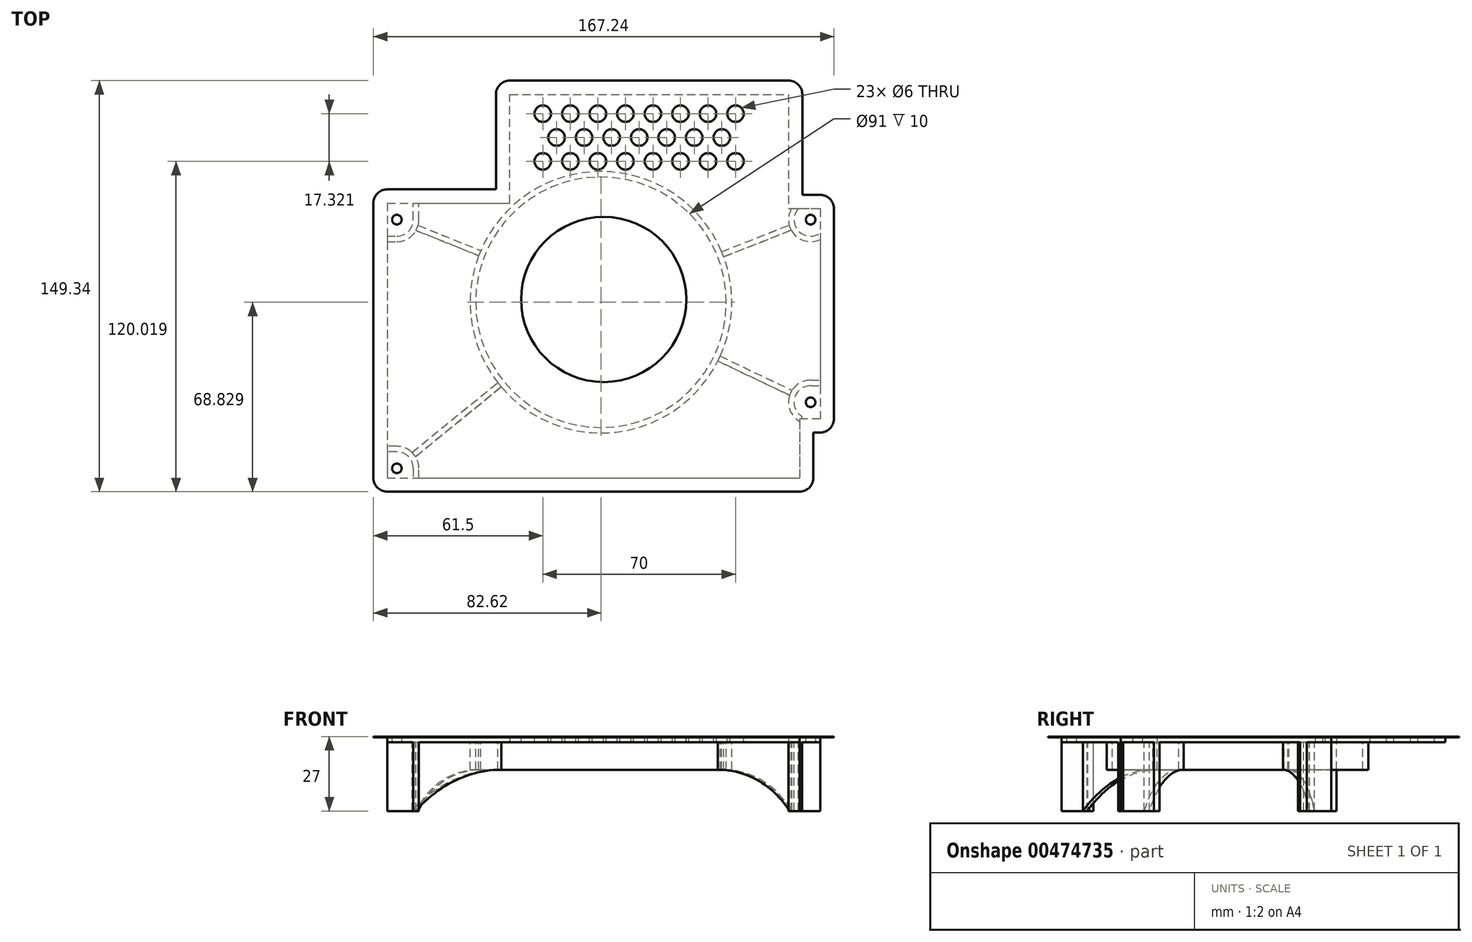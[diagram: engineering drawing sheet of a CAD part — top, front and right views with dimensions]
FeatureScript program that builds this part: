
annotation { "Feature Type Name" : "Feature", "Feature Type Description" : "" }
export const myFeature = defineFeature(function(context is Context, id is Id, definition is map)
    precondition{}
    {
        {
            var Q0;
            Q0=qCreatedBy(makeId("Top.planeOp"),FACE);
            var sketch = newSketch(context, id + "F0", { "sketchPlane" : qUnion([Q0])});
            skLineSegment(sketch, "E0.bottom", {"start": v(0, 0) * mm, "end": v(158.24, 0) * mm, "construction": true});
            skLineSegment(sketch, "E0.top", {"start": v(0, 140.34) * mm, "end": v(158.24, 140.34) * mm, "construction": true});
            skLineSegment(sketch, "E0.left", {"start": v(0, 0) * mm, "end": v(0, 140.34) * mm, "construction": true});
            skLineSegment(sketch, "E0.right", {"start": v(158.24, 0) * mm, "end": v(158.24, 140.34) * mm, "construction": true});
            skLineSegment(sketch, "E1.bottom", {"start": v(45, 139.84) * mm, "end": v(146.24, 139.84) * mm});
            skLineSegment(sketch, "E1.top", {"start": v(0.5, 0.5) * mm, "end": v(150.24, 0.5) * mm});
            skLineSegment(sketch, "E1.left", {"start": v(0.5, 100.34) * mm, "end": v(0.5, 0.5) * mm});
            skLineSegment(sketch, "E1.right", {"start": v(157.74, 98.34) * mm, "end": v(157.74, 22) * mm});
            skCircle(sketch, "E2", {"center": v(4, 94.34) * mm, "radius": 1.75 * mm});
            skCircle(sketch, "E3", {"center": v(4, 4) * mm, "radius": 1.75 * mm});
            skCircle(sketch, "E4", {"center": v(154.24, 94.34) * mm, "radius": 1.75 * mm});
            skCircle(sketch, "E5", {"center": v(154.24, 28) * mm, "radius": 1.75 * mm});
            skLineSegment(sketch, "E6", {"start": v(157.74, 22) * mm, "end": v(150.24, 22) * mm});
            skLineSegment(sketch, "E7", {"start": v(150.24, 22) * mm, "end": v(150.24, 0.5) * mm});
            skLineSegment(sketch, "E8", {"start": v(146.24, 139.84) * mm, "end": v(146.24, 98.34) * mm});
            skLineSegment(sketch, "E9", {"start": v(146.24, 98.34) * mm, "end": v(157.74, 98.34) * mm});
            skLineSegment(sketch, "E10", {"start": v(0.5, 100.34) * mm, "end": v(45, 100.34) * mm});
            skLineSegment(sketch, "E11", {"start": v(45, 100.34) * mm, "end": v(45, 139.84) * mm});
            skCircle(sketch, "E12", {"center": v(79.12, 65.33) * mm, "radius": 44.5 * mm, "construction": true});
            skSolve(sketch);
        }
        {
            var Q0;
            Q0=qSketchRegion(id+"F0",true);
            extrude(context, id + "F1", {"entities" : qUnion([Q0]), "depth" : 2 * mm, "offsetDistance" : 25 * mm});
        }
        {
            var Q0;
            Q0=makeQuery(id+"F1.opExtrude","CAP_FACE",FACE,{"disambiguationData":[OSD([sQuery(id+"F0.wireOp",EDGE,"E1.bottom"),sQuery(id+"F0.wireOp",EDGE,"E1.top"),sQuery(id+"F0.wireOp",EDGE,"E1.left"),sQuery(id+"F0.wireOp",EDGE,"E1.right"),sQuery(id+"F0.wireOp",EDGE,"E2"),sQuery(id+"F0.wireOp",EDGE,"E3"),sQuery(id+"F0.wireOp",EDGE,"E4"),sQuery(id+"F0.wireOp",EDGE,"E5"),sQuery(id+"F0.wireOp",EDGE,"E6"),sQuery(id+"F0.wireOp",EDGE,"E7"),sQuery(id+"F0.wireOp",EDGE,"E8"),sQuery(id+"F0.wireOp",EDGE,"E9"),sQuery(id+"F0.wireOp",EDGE,"E10"),sQuery(id+"F0.wireOp",EDGE,"E11")])],"isStart":true});
            var sketch = newSketch(context, id + "F2", { "sketchPlane" : qUnion([Q0])});
            skCircle(sketch, "E13", {"center": v(78.12, -64.33) * mm, "radius": 44.5 * mm, "construction": true});
            skCircle(sketch, "E14", {"center": v(78.12, -64.33) * mm, "radius": 45.5 * mm});
            skLineSegment(sketch, "E15", {"start": v(120.56, -139.84) * mm, "end": v(122.87, -139.84) * mm});
            skLineSegment(sketch, "E16", {"start": v(4, -94.34) * mm, "end": v(78.12, -64.33) * mm, "construction": true});
            skLineSegment(sketch, "E17", {"start": v(4, -4) * mm, "end": v(78.12, -64.33) * mm, "construction": true});
            skLineSegment(sketch, "E18", {"start": v(154.24, -28) * mm, "end": v(78.12, -64.33) * mm, "construction": true});
            skLineSegment(sketch, "E19", {"start": v(78.12, -64.33) * mm, "end": v(154.24, -94.34) * mm, "construction": true});
            skArc(sketch, "E20", {"start": v(4, -10) * mm, "mid": v(8.24, -8.24) * mm, "end": v(10, -4) * mm});
            skArc(sketch, "E21", {"start": v(40.66, -35.13) * mm, "mid": v(31.15, -57.27) * mm, "end": v(33.73, -81.22) * mm});
            skArc(sketch, "E22", {"start": v(4, -12) * mm, "mid": v(6.98, -11.43) * mm, "end": v(9.52, -9.79) * mm});
            skLineSegment(sketch, "E23", {"start": v(10.79, -8.23) * mm, "end": v(41.92, -33.58) * mm});
            skLineSegment(sketch, "E24", {"start": v(9.52, -9.79) * mm, "end": v(40.66, -35.13) * mm});
            skArc(sketch, "E25.trimOffspring", {"start": v(10.79, -8.23) * mm, "mid": v(11.7, -6.2) * mm, "end": v(12, -4) * mm});
            skArc(sketch, "E26", {"start": v(10, -94.34) * mm, "mid": v(8.24, -90.1) * mm, "end": v(4, -88.34) * mm});
            skLineSegment(sketch, "E27", {"start": v(4, -10) * mm, "end": v(0.5, -10) * mm});
            skLineSegment(sketch, "E28", {"start": v(4, -12) * mm, "end": v(0.5, -12) * mm});
            skLineSegment(sketch, "E29", {"start": v(0.5, -10) * mm, "end": v(0.5, -12) * mm});
            skLineSegment(sketch, "E30", {"start": v(10, -4) * mm, "end": v(10, -0.5) * mm});
            skLineSegment(sketch, "E31", {"start": v(12, -0.5) * mm, "end": v(12, -4) * mm});
            skLineSegment(sketch, "E32", {"start": v(10, -0.5) * mm, "end": v(12, -0.5) * mm});
            skLineSegment(sketch, "E33", {"start": v(0.5, -86.34) * mm, "end": v(4, -86.34) * mm});
            skLineSegment(sketch, "E34", {"start": v(0.5, -88.34) * mm, "end": v(4, -88.34) * mm});
            skLineSegment(sketch, "E35", {"start": v(12, -94.34) * mm, "end": v(12, -100.34) * mm});
            skLineSegment(sketch, "E36", {"start": v(10, -94.34) * mm, "end": v(10, -100.34) * mm});
            skArc(sketch, "E37.trimOffspring", {"start": v(12, -94.34) * mm, "mid": v(11.93, -93.3) * mm, "end": v(11.73, -92.29) * mm});
            skLineSegment(sketch, "E38", {"start": v(0.5, -86.34) * mm, "end": v(0.5, -88.34) * mm});
            skLineSegment(sketch, "E39", {"start": v(10, -100.34) * mm, "end": v(12, -100.34) * mm});
            skLineSegment(sketch, "E40", {"start": v(10.98, -90.43) * mm, "end": v(33.73, -81.22) * mm});
            skLineSegment(sketch, "E41", {"start": v(11.73, -92.29) * mm, "end": v(34.48, -83.08) * mm});
            skArc(sketch, "E42.trimOffspring", {"start": v(10.98, -90.43) * mm, "mid": v(8.05, -87.44) * mm, "end": v(4, -86.34) * mm});
            skArc(sketch, "E43.trimOffspring", {"start": v(34.48, -83.08) * mm, "mid": v(78.34, -111.83) * mm, "end": v(121.93, -82.68) * mm});
            skArc(sketch, "E44", {"start": v(151.17, -22.85) * mm, "mid": v(148.46, -29.6) * mm, "end": v(154.24, -34) * mm});
            skArc(sketch, "E45", {"start": v(150.24, -21.07) * mm, "mid": v(146.76, -25.15) * mm, "end": v(146.65, -30.52) * mm});
            skLineSegment(sketch, "E46", {"start": v(154.24, -34) * mm, "end": v(157.74, -34) * mm});
            skLineSegment(sketch, "E47", {"start": v(154.24, -36) * mm, "end": v(157.74, -36) * mm});
            skLineSegment(sketch, "E48", {"start": v(157.74, -34) * mm, "end": v(157.74, -36) * mm});
            skLineSegment(sketch, "E49", {"start": v(150.24, -21.07) * mm, "end": v(150.24, -22) * mm});
            skLineSegment(sketch, "E50", {"start": v(150.24, -22) * mm, "end": v(151.17, -22) * mm});
            skLineSegment(sketch, "E51", {"start": v(120.55, -42.97) * mm, "end": v(146.65, -30.52) * mm});
            skLineSegment(sketch, "E52", {"start": v(121.4, -44.78) * mm, "end": v(147.5, -32.32) * mm});
            skArc(sketch, "E53.trimOffspring", {"start": v(120.55, -42.97) * mm, "mid": v(83.76, -17.16) * mm, "end": v(41.92, -33.58) * mm});
            skArc(sketch, "E54.trimOffspring", {"start": v(147.5, -32.32) * mm, "mid": v(150.4, -35.02) * mm, "end": v(154.24, -36) * mm});
            skArc(sketch, "E55", {"start": v(157.74, -89.47) * mm, "mid": v(149.78, -90.33) * mm, "end": v(149.77, -98.34) * mm});
            skArc(sketch, "E56", {"start": v(157.74, -87.15) * mm, "mid": v(151.81, -86.72) * mm, "end": v(147.22, -90.5) * mm});
            skLineSegment(sketch, "E57", {"start": v(147.31, -98.34) * mm, "end": v(149.77, -98.34) * mm});
            skLineSegment(sketch, "E58", {"start": v(157.74, -89.47) * mm, "end": v(157.74, -87.15) * mm});
            skLineSegment(sketch, "E59", {"start": v(122.67, -80.82) * mm, "end": v(147.22, -90.5) * mm});
            skLineSegment(sketch, "E60", {"start": v(121.93, -82.68) * mm, "end": v(146.49, -92.36) * mm});
            skArc(sketch, "E61.trimOffspring", {"start": v(122.67, -80.82) * mm, "mid": v(125.6, -62.67) * mm, "end": v(121.4, -44.78) * mm});
            skArc(sketch, "E62.trimOffspring", {"start": v(146.49, -92.36) * mm, "mid": v(146.31, -95.43) * mm, "end": v(147.31, -98.34) * mm});
            skLineSegment(sketch, "E63", {"start": v(151.17, -22) * mm, "end": v(151.17, -22.85) * mm});
            skSolve(sketch);
        }
        {
            var Q0;
            Q0=qSketchRegion(id+"F2",true);
            extrude(context, id + "F3", {"entities" : qUnion([Q0]), "operationType" : NewBodyOperationType.ADD, "depth" : 25 * mm, "offsetDistance" : 25 * mm});
        }
        {
            var Q0;
            Q0=makeQuery(id+"F3.opExtrude","CAP_FACE",FACE,{"disambiguationData":[OSD([sQuery(id+"F2.wireOp",EDGE,"E14"),sQuery(id+"F2.wireOp",EDGE,"E20"),sQuery(id+"F2.wireOp",EDGE,"E21"),sQuery(id+"F2.wireOp",EDGE,"E22"),sQuery(id+"F2.wireOp",EDGE,"E23"),sQuery(id+"F2.wireOp",EDGE,"E24"),sQuery(id+"F2.wireOp",EDGE,"E25.trimOffspring"),sQuery(id+"F2.wireOp",EDGE,"E26"),sQuery(id+"F2.wireOp",EDGE,"E27"),sQuery(id+"F2.wireOp",EDGE,"E28"),sQuery(id+"F2.wireOp",EDGE,"E29"),sQuery(id+"F2.wireOp",EDGE,"E30"),sQuery(id+"F2.wireOp",EDGE,"E31"),sQuery(id+"F2.wireOp",EDGE,"E32"),sQuery(id+"F2.wireOp",EDGE,"E33"),sQuery(id+"F2.wireOp",EDGE,"E34"),sQuery(id+"F2.wireOp",EDGE,"E35"),sQuery(id+"F2.wireOp",EDGE,"E36"),sQuery(id+"F2.wireOp",EDGE,"E37.trimOffspring"),sQuery(id+"F2.wireOp",EDGE,"E38"),sQuery(id+"F2.wireOp",EDGE,"E39"),sQuery(id+"F2.wireOp",EDGE,"E40"),sQuery(id+"F2.wireOp",EDGE,"E41"),sQuery(id+"F2.wireOp",EDGE,"E42.trimOffspring"),sQuery(id+"F2.wireOp",EDGE,"E43.trimOffspring"),sQuery(id+"F2.wireOp",EDGE,"E44"),sQuery(id+"F2.wireOp",EDGE,"E45"),sQuery(id+"F2.wireOp",EDGE,"E46"),sQuery(id+"F2.wireOp",EDGE,"E47"),sQuery(id+"F2.wireOp",EDGE,"E48"),sQuery(id+"F2.wireOp",EDGE,"E49"),sQuery(id+"F2.wireOp",EDGE,"E50"),sQuery(id+"F2.wireOp",EDGE,"E51"),sQuery(id+"F2.wireOp",EDGE,"E52"),sQuery(id+"F2.wireOp",EDGE,"E53.trimOffspring"),sQuery(id+"F2.wireOp",EDGE,"E54.trimOffspring"),sQuery(id+"F2.wireOp",EDGE,"E55"),sQuery(id+"F2.wireOp",EDGE,"E56"),sQuery(id+"F2.wireOp",EDGE,"E57"),sQuery(id+"F2.wireOp",EDGE,"E58"),sQuery(id+"F2.wireOp",EDGE,"E59"),sQuery(id+"F2.wireOp",EDGE,"E60"),sQuery(id+"F2.wireOp",EDGE,"E61.trimOffspring"),sQuery(id+"F2.wireOp",EDGE,"E62.trimOffspring"),sQuery(id+"F2.wireOp",EDGE,"E63")])],"isStart":false});
            var sketch = newSketch(context, id + "F4", { "sketchPlane" : qUnion([Q0])});
            skCircle(sketch, "E64", {"center": v(78.12, -64.33) * mm, "radius": 45.5 * mm});
            skCircle(sketch, "E65", {"center": v(78.12, -64.33) * mm, "radius": 47.5 * mm});
            skSolve(sketch);
        }
        {
            var Q0;
            Q0=qSketchRegion(id+"F4",true);
            extrude(context, id + "F5", {"entities" : qUnion([Q0]), "operationType" : NewBodyOperationType.REMOVE, "oppositeDirection" : true, "depth" : 15 * mm, "offsetDistance" : 25 * mm});
        }
        {
            var Q0;
            Q0=makeQuery(id+"F3.opExtrude","SWEPT_FACE",FACE,{"disambiguationData":[OSD([sQuery(id+"F2.wireOp",EDGE,"E24")])]});
            var sketch = newSketch(context, id + "F6", { "sketchPlane" : qUnion([Q0])});
            skArc(sketch, "E66", {"start": v(-13.56, -25) * mm, "mid": v(-32.28, -13.87) * mm, "end": v(-53.7, -10) * mm});
            skLineSegment(sketch, "E67", {"start": v(-53.7, -10) * mm, "end": v(-13.56, -10) * mm, "construction": true});
            skLineSegment(sketch, "E68", {"start": v(-53.7, -10) * mm, "end": v(-53.7, -25) * mm});
            skLineSegment(sketch, "E69", {"start": v(-53.7, -25) * mm, "end": v(-13.56, -25) * mm});
            skSolve(sketch);
        }
        {
            var Q0;
            Q0=qSketchRegion(id+"F6",true);
            extrude(context, id + "F7", {"entities" : qUnion([Q0]), "operationType" : NewBodyOperationType.REMOVE, "endBound" : BoundingType.UP_TO_NEXT, "oppositeDirection" : true, "depth" : 25 * mm, "offsetDistance" : 25 * mm});
        }
        {
            var Q0;
            Q0=makeQuery(id+"F3.opExtrude","SWEPT_FACE",FACE,{"disambiguationData":[OSD([sQuery(id+"F2.wireOp",EDGE,"E41")])]});
            var sketch = newSketch(context, id + "F8", { "sketchPlane" : qUnion([Q0])});
            skArc(sketch, "E70", {"start": v(23.76, -25) * mm, "mid": v(13.6, -14.05) * mm, "end": v(-0.78, -10) * mm});
            skLineSegment(sketch, "E71", {"start": v(-0.78, -10) * mm, "end": v(23.76, -10) * mm, "construction": true});
            skLineSegment(sketch, "E72", {"start": v(23.76, -25) * mm, "end": v(-0.78, -25) * mm});
            skLineSegment(sketch, "E73", {"start": v(-0.78, -25) * mm, "end": v(-0.78, -10) * mm});
            skSolve(sketch);
        }
        {
            var Q0;
            Q0=qSketchRegion(id+"F8",true);
            extrude(context, id + "F9", {"entities" : qUnion([Q0]), "operationType" : NewBodyOperationType.REMOVE, "endBound" : BoundingType.UP_TO_NEXT, "oppositeDirection" : true, "depth" : 25 * mm, "offsetDistance" : 25 * mm});
        }
        {
            var Q0;
            Q0=makeQuery(id+"F3.opExtrude","SWEPT_FACE",FACE,{"disambiguationData":[OSD([sQuery(id+"F2.wireOp",EDGE,"E60")])]});
            var sketch = newSketch(context, id + "F10", { "sketchPlane" : qUnion([Q0])});
            skLineSegment(sketch, "E74", {"start": v(-143.76, -10) * mm, "end": v(-143.76, -25) * mm});
            skLineSegment(sketch, "E75", {"start": v(-143.76, -25) * mm, "end": v(-170.16, -25) * mm});
            skLineSegment(sketch, "E76", {"start": v(-143.76, -10) * mm, "end": v(-170.16, -10) * mm, "construction": true});
            skArc(sketch, "E77", {"start": v(-143.76, -10) * mm, "mid": v(-158.94, -14.01) * mm, "end": v(-170.16, -25) * mm});
            skSolve(sketch);
        }
        {
            var Q0;
            Q0=qSketchRegion(id+"F10",true);
            extrude(context, id + "F11", {"entities" : qUnion([Q0]), "operationType" : NewBodyOperationType.REMOVE, "endBound" : BoundingType.UP_TO_NEXT, "oppositeDirection" : true, "depth" : 25 * mm, "offsetDistance" : 25 * mm});
        }
        {
            var Q0;
            Q0=makeQuery(id+"F3.opExtrude","SWEPT_FACE",FACE,{"disambiguationData":[OSD([sQuery(id+"F2.wireOp",EDGE,"E52")])]});
            var sketch = newSketch(context, id + "F12", { "sketchPlane" : qUnion([Q0])});
            skLineSegment(sketch, "E78", {"start": v(-90.28, -10) * mm, "end": v(-90.28, -25) * mm});
            skLineSegment(sketch, "E79", {"start": v(-90.28, -25) * mm, "end": v(-119.2, -25) * mm});
            skLineSegment(sketch, "E80", {"start": v(-90.28, -10) * mm, "end": v(-119.2, -10) * mm, "construction": true});
            skArc(sketch, "E81", {"start": v(-90.28, -10) * mm, "mid": v(-106.57, -13.97) * mm, "end": v(-119.2, -25) * mm});
            skSolve(sketch);
        }
        {
            var Q0;
            Q0=qSketchRegion(id+"F12",true);
            extrude(context, id + "F13", {"entities" : qUnion([Q0]), "operationType" : NewBodyOperationType.REMOVE, "endBound" : BoundingType.UP_TO_NEXT, "oppositeDirection" : true, "depth" : 25 * mm, "offsetDistance" : 25 * mm});
        }
        {
            var Q0;
            Q0=makeQuery(id+"F1.opExtrude","CAP_FACE",FACE,{"disambiguationData":[OSD([sQuery(id+"F0.wireOp",EDGE,"E1.bottom"),sQuery(id+"F0.wireOp",EDGE,"E1.top"),sQuery(id+"F0.wireOp",EDGE,"E1.left"),sQuery(id+"F0.wireOp",EDGE,"E1.right"),sQuery(id+"F0.wireOp",EDGE,"E2"),sQuery(id+"F0.wireOp",EDGE,"E3"),sQuery(id+"F0.wireOp",EDGE,"E4"),sQuery(id+"F0.wireOp",EDGE,"E5"),sQuery(id+"F0.wireOp",EDGE,"E6"),sQuery(id+"F0.wireOp",EDGE,"E7"),sQuery(id+"F0.wireOp",EDGE,"E8"),sQuery(id+"F0.wireOp",EDGE,"E9"),sQuery(id+"F0.wireOp",EDGE,"E10"),sQuery(id+"F0.wireOp",EDGE,"E11")])],"isStart":false});
            var sketch = newSketch(context, id + "F14", { "sketchPlane" : qUnion([Q0])});
            skCircle(sketch, "E82", {"center": v(57, 132.84) * mm, "radius": 3 * mm});
            skCircle(sketch, "E83.1.0.0", {"center": v(67, 132.84) * mm, "radius": 3 * mm});
            skCircle(sketch, "E83.2.0.0", {"center": v(77, 132.84) * mm, "radius": 3 * mm});
            skCircle(sketch, "E83.3.0.0", {"center": v(87, 132.84) * mm, "radius": 3 * mm});
            skCircle(sketch, "E83.4.0.0", {"center": v(97, 132.84) * mm, "radius": 3 * mm});
            skCircle(sketch, "E83.5.0.0", {"center": v(107, 132.84) * mm, "radius": 3 * mm});
            skCircle(sketch, "E83.6.0.0", {"center": v(117, 132.84) * mm, "radius": 3 * mm});
            skCircle(sketch, "E83.7.0.0", {"center": v(127, 132.84) * mm, "radius": 3 * mm});
            skLineSegment(sketch, "E83.direction1", {"start": v(57, 132.84) * mm, "end": v(67, 132.84) * mm, "construction": true});
            skLineSegment(sketch, "E84", {"start": v(57, 132.84) * mm, "end": v(62, 124.18) * mm, "construction": true});
            skLineSegment(sketch, "E85", {"start": v(62, 124.18) * mm, "end": v(67, 132.84) * mm, "construction": true});
            skCircle(sketch, "E86", {"center": v(62, 124.18) * mm, "radius": 3 * mm});
            skCircle(sketch, "E87.1.0.0", {"center": v(72, 124.18) * mm, "radius": 3 * mm});
            skCircle(sketch, "E87.2.0.0", {"center": v(82, 124.18) * mm, "radius": 3 * mm});
            skCircle(sketch, "E87.3.0.0", {"center": v(92, 124.18) * mm, "radius": 3 * mm});
            skCircle(sketch, "E87.4.0.0", {"center": v(102, 124.18) * mm, "radius": 3 * mm});
            skCircle(sketch, "E87.5.0.0", {"center": v(112, 124.18) * mm, "radius": 3 * mm});
            skCircle(sketch, "E87.6.0.0", {"center": v(122, 124.18) * mm, "radius": 3 * mm});
            skLineSegment(sketch, "E87.direction1", {"start": v(62, 124.18) * mm, "end": v(72, 124.18) * mm, "construction": true});
            skLineSegment(sketch, "E88", {"start": v(62, 124.18) * mm, "end": v(57, 115.52) * mm, "construction": true});
            skLineSegment(sketch, "E89", {"start": v(57, 115.52) * mm, "end": v(67, 115.52) * mm, "construction": true});
            skLineSegment(sketch, "E90", {"start": v(67, 115.52) * mm, "end": v(62, 124.18) * mm, "construction": true});
            skCircle(sketch, "E91", {"center": v(57, 115.52) * mm, "radius": 3 * mm});
            skCircle(sketch, "E92.1.0.0", {"center": v(67, 115.52) * mm, "radius": 3 * mm});
            skCircle(sketch, "E92.2.0.0", {"center": v(77, 115.52) * mm, "radius": 3 * mm});
            skCircle(sketch, "E92.3.0.0", {"center": v(87, 115.52) * mm, "radius": 3 * mm});
            skCircle(sketch, "E92.4.0.0", {"center": v(97, 115.52) * mm, "radius": 3 * mm});
            skCircle(sketch, "E92.5.0.0", {"center": v(107, 115.52) * mm, "radius": 3 * mm});
            skCircle(sketch, "E92.6.0.0", {"center": v(117, 115.52) * mm, "radius": 3 * mm});
            skCircle(sketch, "E92.7.0.0", {"center": v(127, 115.52) * mm, "radius": 3 * mm});
            skCircle(sketch, "E93", {"center": v(79.12, 65.33) * mm, "radius": 30 * mm});
            skSolve(sketch);
        }
        {
            var Q0;
            Q0=qSketchRegion(id+"F14",true);
            extrude(context, id + "F15", {"entities" : qUnion([Q0]), "operationType" : NewBodyOperationType.REMOVE, "endBound" : BoundingType.UP_TO_NEXT, "oppositeDirection" : true, "depth" : 25 * mm, "offsetDistance" : 25 * mm});
        }
        {
            var Q0;
            Q0=makeQuery(id+"F1.opExtrude","CAP_FACE",FACE,{"disambiguationData":[OSD([sQuery(id+"F0.wireOp",EDGE,"E1.bottom"),sQuery(id+"F0.wireOp",EDGE,"E1.top"),sQuery(id+"F0.wireOp",EDGE,"E1.left"),sQuery(id+"F0.wireOp",EDGE,"E1.right"),sQuery(id+"F0.wireOp",EDGE,"E2"),sQuery(id+"F0.wireOp",EDGE,"E3"),sQuery(id+"F0.wireOp",EDGE,"E4"),sQuery(id+"F0.wireOp",EDGE,"E5"),sQuery(id+"F0.wireOp",EDGE,"E6"),sQuery(id+"F0.wireOp",EDGE,"E7"),sQuery(id+"F0.wireOp",EDGE,"E8"),sQuery(id+"F0.wireOp",EDGE,"E9"),sQuery(id+"F0.wireOp",EDGE,"E10"),sQuery(id+"F0.wireOp",EDGE,"E11")])],"isStart":false});
            var sketch = newSketch(context, id + "F16", { "sketchPlane" : qUnion([Q0])});
            skLineSegment(sketch, "E94", {"start": v(0.5, 100.34) * mm, "end": v(0.5, 0.5) * mm});
            skLineSegment(sketch, "E95", {"start": v(0.5, 0.5) * mm, "end": v(150.24, 0.5) * mm});
            skLineSegment(sketch, "E96", {"start": v(150.24, 0.5) * mm, "end": v(150.24, 22) * mm});
            skLineSegment(sketch, "E97", {"start": v(150.24, 22) * mm, "end": v(157.74, 22) * mm});
            skLineSegment(sketch, "E98", {"start": v(157.74, 22) * mm, "end": v(157.74, 98.34) * mm});
            skLineSegment(sketch, "E99", {"start": v(157.74, 98.34) * mm, "end": v(146.24, 98.34) * mm});
            skLineSegment(sketch, "E100", {"start": v(146.24, 98.34) * mm, "end": v(146.24, 139.84) * mm});
            skLineSegment(sketch, "E101", {"start": v(146.24, 139.84) * mm, "end": v(45, 139.84) * mm});
            skLineSegment(sketch, "E102", {"start": v(45, 139.84) * mm, "end": v(45, 100.34) * mm});
            skLineSegment(sketch, "E103", {"start": v(45, 100.34) * mm, "end": v(0.5, 100.34) * mm});
            skLineSegment(sketch, "E104", {"start": v(40, 105.34) * mm, "end": v(0.5, 105.34) * mm});
            skLineSegment(sketch, "E105", {"start": v(40, 105.34) * mm, "end": v(40, 139.84) * mm});
            skLineSegment(sketch, "E106", {"start": v(45, 144.84) * mm, "end": v(146.24, 144.84) * mm});
            skLineSegment(sketch, "E107", {"start": v(151.24, 139.84) * mm, "end": v(151.24, 103.34) * mm});
            skLineSegment(sketch, "E108", {"start": v(151.24, 103.34) * mm, "end": v(157.74, 103.34) * mm});
            skLineSegment(sketch, "E109", {"start": v(162.74, 98.34) * mm, "end": v(162.74, 22) * mm});
            skLineSegment(sketch, "E110", {"start": v(155.24, 17) * mm, "end": v(157.74, 17) * mm});
            skLineSegment(sketch, "E111", {"start": v(155.24, 17) * mm, "end": v(155.24, 0.5) * mm});
            skLineSegment(sketch, "E112", {"start": v(0.5, -4.5) * mm, "end": v(150.24, -4.5) * mm});
            skLineSegment(sketch, "E113", {"start": v(-4.5, 100.34) * mm, "end": v(-4.5, 0.5) * mm});
            skArc(sketch, "E114", {"start": v(45, 144.84) * mm, "mid": v(41.46, 143.38) * mm, "end": v(40, 139.84) * mm});
            skArc(sketch, "E115", {"start": v(0.5, 105.34) * mm, "mid": v(-3.04, 103.88) * mm, "end": v(-4.5, 100.34) * mm});
            skArc(sketch, "E116", {"start": v(151.24, 139.84) * mm, "mid": v(149.78, 143.38) * mm, "end": v(146.24, 144.84) * mm});
            skArc(sketch, "E117", {"start": v(162.74, 98.34) * mm, "mid": v(161.28, 101.88) * mm, "end": v(157.74, 103.34) * mm});
            skArc(sketch, "E118", {"start": v(157.74, 17) * mm, "mid": v(161.28, 18.46) * mm, "end": v(162.74, 22) * mm});
            skArc(sketch, "E119", {"start": v(150.24, -4.5) * mm, "mid": v(153.78, -3.04) * mm, "end": v(155.24, 0.5) * mm});
            skArc(sketch, "E120", {"start": v(-4.5, 0.5) * mm, "mid": v(-3.04, -3.04) * mm, "end": v(0.5, -4.5) * mm});
            skSolve(sketch);
        }
        {
            var Q0;
            Q0 = qSketchRegion(id + "F16", true);
            extrude(context, id + "F17", {"entities" : qUnion([Q0]), "operationType" : NewBodyOperationType.ADD, "oppositeDirection" : true, "depth" : 0.2 * mm, "offsetDistance" : 25 * mm});
        }
    });
